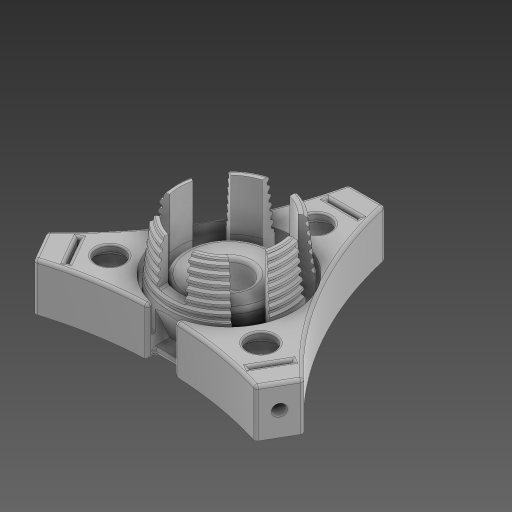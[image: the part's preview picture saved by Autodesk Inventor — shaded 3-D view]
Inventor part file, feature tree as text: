
AUTODESK INVENTOR PART (.ipt)
format: ipt  version: 2024 (Build 280153000, 153)  size: 1,769,984 bytes
history: native  units: mm
features: sketch x18, extrude x13, fillet x10, chamfer x4, hole x3, pattern_circular x3, draft x2, helix x2, plane x2, projected_geometry x2
ambient origin geometry x8: Origin, YZ Plane, XZ Plane, XY Plane, X Axis, Y Axis, Z Axis, Center Point
bodies: Solid1 (feature_tree)
feature tree (59):
  extrude  "Extrusion1"  Depth=29.5mm
  draft  "FaceDraft1"
  sketch  "Sketch2"  dims[d7=6.806784mm d8=0.55605mm]
  helix  "Coil1"  [1 undecoded]
  helix  "Coil2"  [1 undecoded]
  extrude  "Extrusion2"  Depth=0.55605mm
  extrude  "Extrusion3"  TaperAngle=0.0deg  [1 undecoded]
  fillet  "Fillet1"  [1 undecoded]
  chamfer  "Chamfer1"  Distance=0.3mm Angle=45.0deg
  plane  "Work Plane1"
  extrude  "Extrusion4"  TaperAngle=0.0deg  [1 undecoded]
  extrude  "Extrusion8"  Depth=60.0mm TaperAngle=360.0deg
  hole  "Hole2"  [1 undecoded]
  sketch  "Sketch13"  dims[d58=6.0mm d65=60.0mm d67=360.0deg]
  extrude  "Extrusion11"  Depth=10.0mm TaperAngle=0.0deg
  hole  "Bearing Hole"  [1 undecoded]
  pattern_circular  "Circular Pattern4"  Count=3 Angle=360.0deg
  extrude  "Extrusion13"  Depth=7.0mm TaperAngle=0.0deg
  sketch  "Sketch20"  dims[d126=6.804mm d127=6.0mm d128=9.829mm d129=8.89mm d130=90.0deg d131=8.0mm d132=20.594885mm d133=22.0mm d134=30.0mm d135=360.0deg]
  extrude  "Extrusion14"  Depth=1.5mm TaperAngle=45.0deg
  sketch  "Sketch18"  dims[d124=34.0mm]
  fillet  "Fillet9"  Radius=0.24mm
  chamfer  "Chamfer4"  [1 undecoded]
  chamfer  "Chamfer5"  Distance=2.0mm
  fillet  "Fillet11"  Radius=34.767mm
  draft  "FaceDraft2"
  fillet  "Fillet13"  Radius=9.0mm
  extrude  "Extrusion15"  TaperAngle=30.0deg  [1 undecoded]
  hole  "Hole5"  [1 undecoded]
  pattern_circular  "Circular Pattern5"  Count=3 Angle=360.0deg
  plane  "Work Plane4"
  extrude  "Extrusion16"  Depth=0.75mm
  fillet  "Fillet14"  [1 undecoded]
  fillet  "Fillet16"  Radius=0.75mm
  extrude  "Extrusion17"  Depth=0.75mm
  extrude  "Extrusion19"  Depth=0.75mm
  fillet  "Fillet17"  Radius=22.0mm
  fillet  "Fillet18"  Radius=31.0mm
  fillet  "Fillet19"  Radius=7.0mm
  extrude  "Extrusion20"  Depth=0.75mm
  fillet  "Fillet20"  Radius=9.0mm
  chamfer  "Chamfer6"  Distance=1.0mm
  pattern_circular  "Circular Pattern6"  [2 undecoded]
  sketch  "Sketch1"  dims[d0=24.7mm d1=29.5mm d2=12.875mm d3=0.0mm d4=1.047198mm]
  projected_geometry  "Projected Loop1"
  sketch  "Sketch3"  dims[d9=6.806784mm]
  sketch  "Sketch4"  dims[d10=2.0mm d11=10.0mm d12=70.0mm d13=-1.047198mm d14=90.0deg d15=90.0deg d16=0.0mm d17=0.0mm d18=0.6mm]
  sketch  "Sketch5"  dims[d19=2.0mm d20=10.0mm d21=10.0mm d22=1.047198mm d23=90.0deg d24=90.0deg d25=0.0mm d26=0.0mm d27=0.0mm d28=0.0mm d29=0.0mm d30=0.0mm]
  sketch  "Sketch10"  dims[d31=0.6mm d32=0.3mm d33=2.0mm d34=45.0deg]
  sketch  "Sketch11"  dims[d36=-2.0mm d42=0.0mm d43=0.0mm]
  sketch  "Sketch15"  dims[d91=33.0mm d92=12.0mm d93=0.0mm]
  sketch  "Sketch17"  dims[d94=5.3mm d95=6.0mm d96=10.0mm d97=7.0mm d98=90.0deg d99=8.0mm d100=20.594885mm d122=10.0mm d123=0.0mm]
  sketch  "Sketch21"  dims[d146=11.34464mm d147=7.0mm d148=0.0mm]
  sketch  "Sketch22"  dims[d150=1.0mm d151=1.5mm d152=2.0mm d153=45.0deg]
  sketch  "Sketch25"  dims[d154=0.5mm d155=2.0mm d156=45.0deg d158=0.24mm]
  sketch  "Sketch26"  dims[d160=1.25mm d161=0.0mm d162=0.0mm]
  sketch  "Sketch28"  dims[d163=30.0deg]
  sketch  "Sketch29"  dims[d164=0.5mm d165=2.0mm d166=34.767mm d167=9.0mm d168=30.0deg d169=7.0mm d170=0.0mm d171=3.0mm d172=6.0mm d173=9.779mm d174=7.62mm d175=90.0deg d176=7.0mm d177=0.0mm d179=30.0mm d180=360.0deg d182=16.0mm d183=0.0mm d184=0.0mm d185=0.75mm d187=0.4mm d188=25.0mm d189=22.0mm d190=31.0mm d191=7.0mm d192=0.0mm d193=32.8mm d208=9.0mm d209=0.0mm d210=1.0mm d211=0.25mm d212=0.5mm d213=7.0mm d214=60.0mm d216=360.0deg d218=8.0mm d219=6.0mm d220=0.6mm d221=0.3mm d222=0.0mm d223=0.0mm d224=0.75mm d225=0.75mm d226=2.0mm d227=45.0deg d228=30.0mm d229=360.0deg d231=6.0mm]
  projected_geometry  "Project Cut Edges3"
note: 13 required parameter values undecoded (feature->parameter linkage not recoverable at this tier; creation-order binding heuristic only, values carry confidence <= 0.55)
